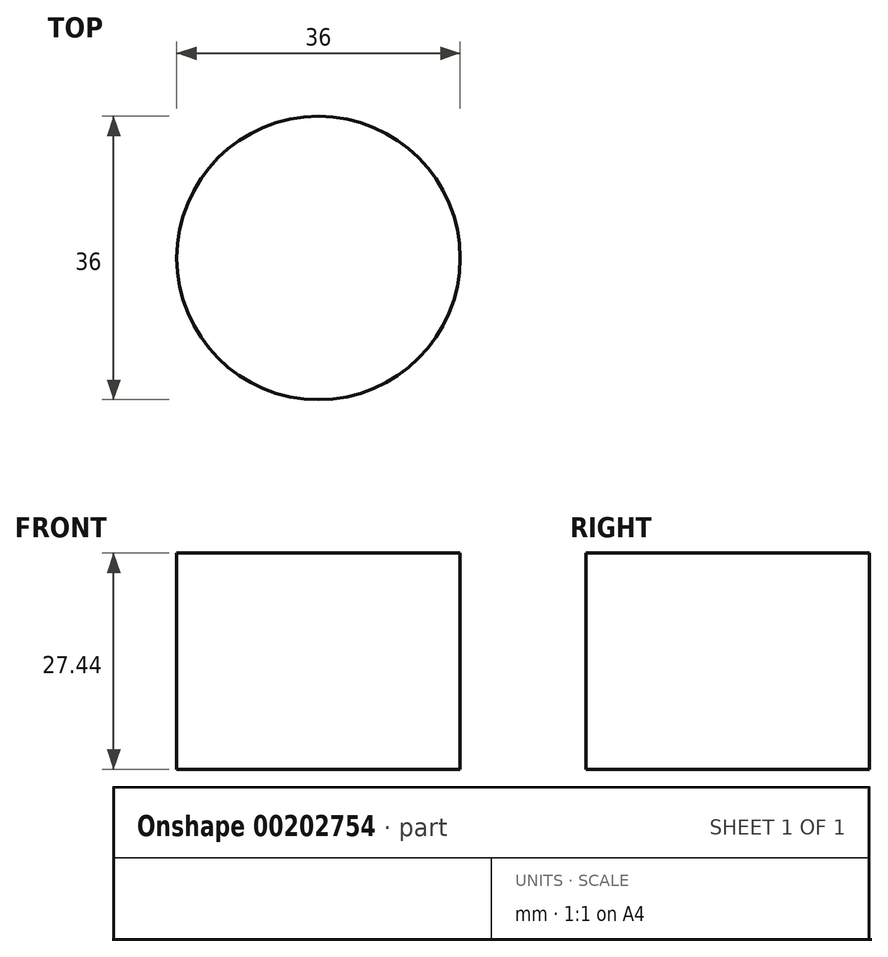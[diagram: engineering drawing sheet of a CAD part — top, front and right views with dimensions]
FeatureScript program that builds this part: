
annotation { "Feature Type Name" : "Feature", "Feature Type Description" : "" }
export const myFeature = defineFeature(function(context is Context, id is Id, definition is map)
    precondition{}
    {
        {
            var Q0;
            Q0=qCreatedBy(makeId("Front.planeOp"),FACE);
            var sketch = newSketch(context, id + "F0", { "sketchPlane" : qUnion([Q0])});
            skLineSegment(sketch, "E0.right", {"start": v(11.1, 48.56) * mm, "end": v(11.1, -21.44) * mm});
            skLineSegment(sketch, "E1.0", {"start": v(-6.9, 46) * mm, "end": v(-6.9, 18.56) * mm});
            skLineSegment(sketch, "E2.bottom", {"start": v(-6.9, 18.56) * mm, "end": v(11.1, 18.56) * mm});
            skLineSegment(sketch, "E2.top", {"start": v(-6.9, 46) * mm, "end": v(11.1, 46) * mm});
            skLineSegment(sketch, "E2.left", {"start": v(-6.9, 18.56) * mm, "end": v(-6.9, 46) * mm});
            skLineSegment(sketch, "E2.right", {"start": v(11.1, 18.56) * mm, "end": v(11.1, 46) * mm});
            skSolve(sketch);
        }
        {
            var Q0;
            Q0=qSketchRegion(id+"F0",true);
            var Q1;
            Q1=sQuery(id+"F0.wireOp",EDGE,"E0.right");
            revolve(context, id + "F1", {"entities" : qUnion([Q0]), "axis" : qUnion([Q1]), "revolveType" : RevolveType.FULL});
        }
    });
